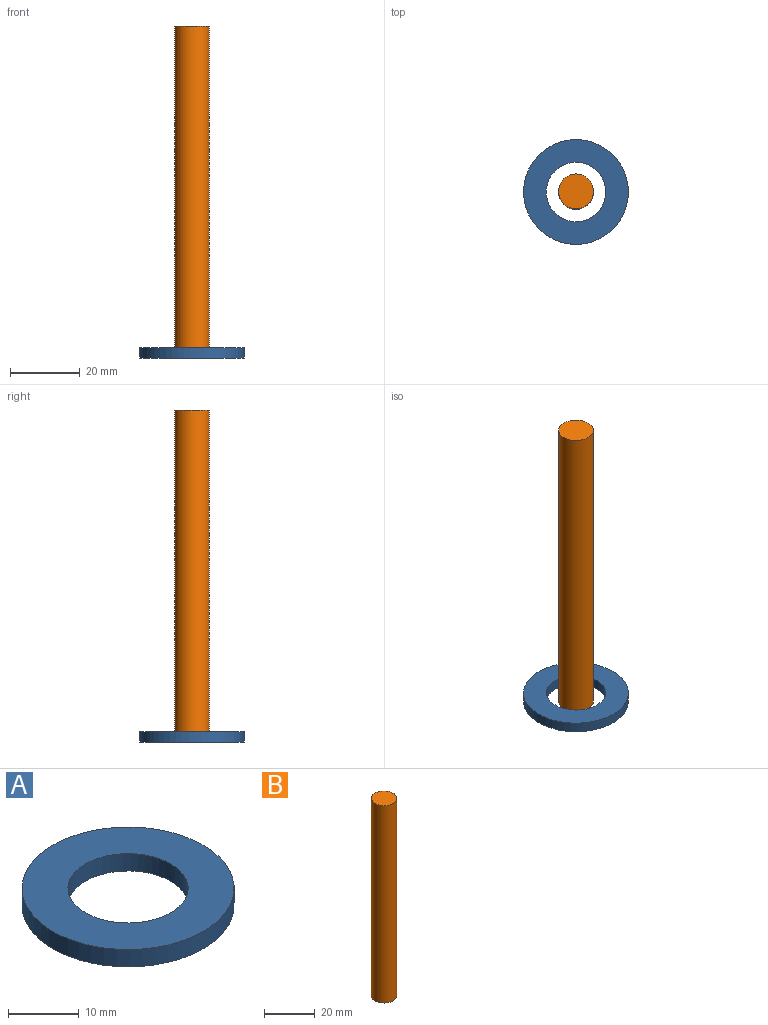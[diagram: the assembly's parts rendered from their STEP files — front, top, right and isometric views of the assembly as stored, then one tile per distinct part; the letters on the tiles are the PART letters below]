
ASSEMBLY  parts=2 mates=1
PART A: 4 faces, bbox 30x30x3 mm
  f0: cylinder r=8.5mm len=17mm, axis (0,0,-1), area 160.2mm2, adj f2,f3
  f1: cylinder r=15mm len=30mm, axis (0,0,-1), area 282.7mm2, adj f2,f3
  f2: plane 30x30mm, normal (0,0,1), area 479.9mm2, adj f0,f1
  f3: plane 30x30mm, normal (0,0,-1), area 479.9mm2, adj f0,f1
PART B: 3 faces, bbox 10x10x95 mm
  f0: cylinder r=5mm len=95mm, axis (0,0,-1), area 2984.5mm2, adj f1,f2
  f1: plane 10x10mm, normal (0,0,1), area 78.5mm2, adj f0
  f2: plane 10x10mm, normal (0,0,-1), area 78.5mm2, adj f0
PLACE A t=(-0.74,0,-4.75)mm
PLACE B t=(-0.74,0,-4.75)mm
MATE fastened A.f1 <-> B.f0  axis (0,0,-1) through (-0.74,0,-4.75)mm
